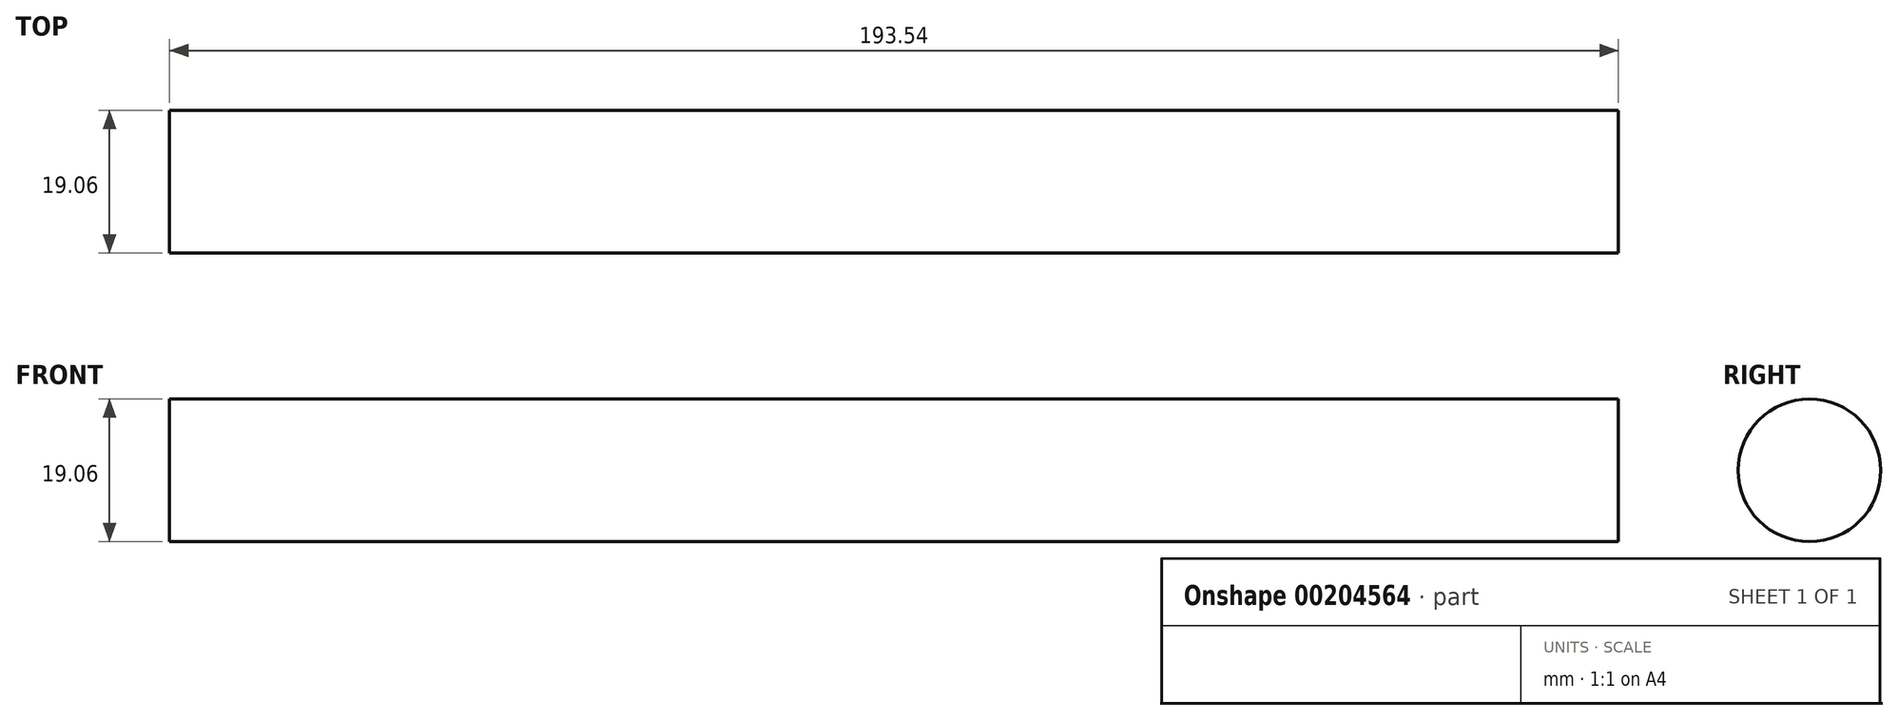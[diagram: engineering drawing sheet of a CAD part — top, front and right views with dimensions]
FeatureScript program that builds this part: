
annotation { "Feature Type Name" : "Feature", "Feature Type Description" : "" }
export const myFeature = defineFeature(function(context is Context, id is Id, definition is map)
    precondition{}
    {
        {
            var Q0;
            Q0=qCreatedBy(makeId("Right.planeOp"),FACE);
            var sketch = newSketch(context, id + "F0", { "sketchPlane" : qUnion([Q0])});
            skCircle(sketch, "E0", {"center": v(0, 0) * mm, "radius": 9.53 * mm});
            skSolve(sketch);
        }
        {
            var Q0;
            Q0 = qSketchRegion(id + "F0", true);
            extrude(context, id + "F1", {"entities" : qUnion([Q0]), "endBound" : BoundingType.SYMMETRIC, "depth" : 193.55 * mm});
        }
    });
